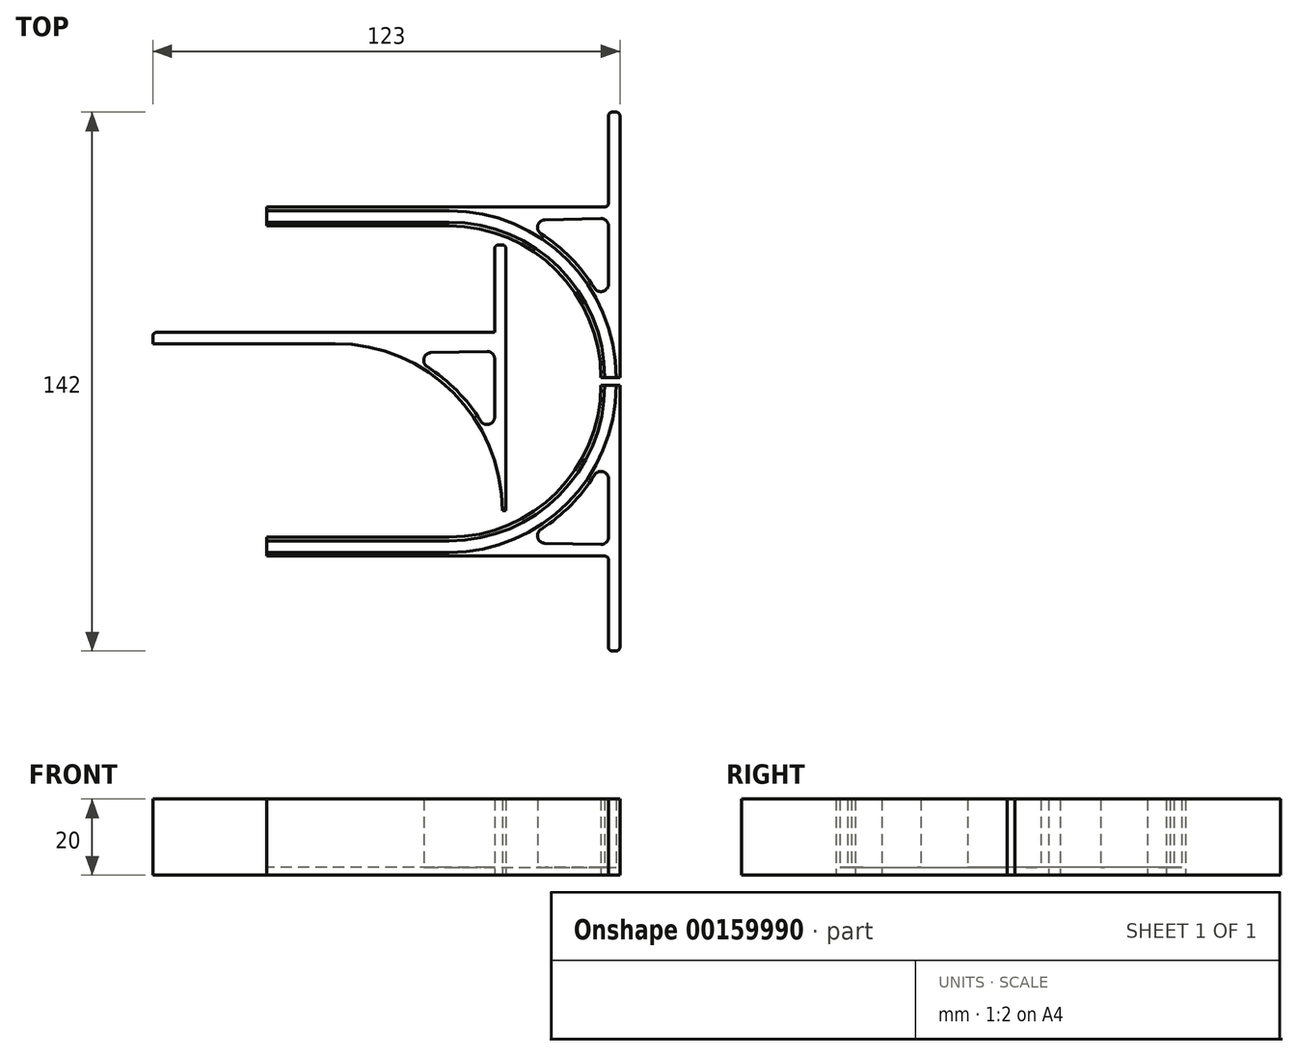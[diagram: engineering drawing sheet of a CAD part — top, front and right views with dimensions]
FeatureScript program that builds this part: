
annotation { "Feature Type Name" : "Feature", "Feature Type Description" : "" }
export const myFeature = defineFeature(function(context is Context, id is Id, definition is map)
    precondition{}
    {
        {
            var Q0;
            Q0=qCreatedBy(makeId("Top.planeOp"),FACE);
            var sketch = newSketch(context, id + "F0", { "sketchPlane" : qUnion([Q0])});
            skLineSegment(sketch, "E0", {"start": v(0, 0) * mm, "end": v(-40, 0) * mm, "construction": true});
            skLineSegment(sketch, "E1", {"start": v(-40, -40) * mm, "end": v(-88, -40) * mm});
            skLineSegment(sketch, "E2", {"start": v(-40, 0) * mm, "end": v(-40, -40) * mm, "construction": true});
            skArc(sketch, "E3", {"start": v(-40, -40) * mm, "mid": v(-11.72, -28.28) * mm, "end": v(0, 0) * mm});
            skLineSegment(sketch, "E4", {"start": v(-88, -40) * mm, "end": v(-88, -45) * mm});
            skLineSegment(sketch, "E5", {"start": v(0, 0) * mm, "end": v(5, 0) * mm});
            skLineSegment(sketch, "E6", {"start": v(5, 0) * mm, "end": v(5, -70) * mm});
            skLineSegment(sketch, "E7", {"start": v(-88, -45) * mm, "end": v(2, -45) * mm});
            skLineSegment(sketch, "E8", {"start": v(2, -45) * mm, "end": v(2, -70) * mm});
            skLineSegment(sketch, "E9", {"start": v(2, -70) * mm, "end": v(5, -70) * mm});
            skSolve(sketch);
        }
        {
            var Q0;
            Q0 = qSketchRegion(id + "F0", true);
            extrude(context, id + "F1", {"entities" : qUnion([Q0]), "depth" : 2 * mm});
        }
        {
            var Q0;
            Q0=makeQuery(id+"F1.opExtrude","CAP_FACE",FACE,{"disambiguationData":[OSD([sQuery(id+"F0.wireOp",EDGE,"E1"),sQuery(id+"F0.wireOp",EDGE,"E3"),sQuery(id+"F0.wireOp",EDGE,"E4"),sQuery(id+"F0.wireOp",EDGE,"E5"),sQuery(id+"F0.wireOp",EDGE,"E6"),sQuery(id+"F0.wireOp",EDGE,"Kue0VMO2-bRpy-jYA9-I0cy-11uejcIptspo"),sQuery(id+"F0.wireOp",EDGE,"twIMW08o-vE7x-7cyn-jqzq-1YqOCdcAmMuu"),sQuery(id+"F0.wireOp",EDGE,"zMnDsJVE-qmB4-Xr0M-Avi3-cOn6qpQtWDXG")])],"isStart":false});
            var sketch = newSketch(context, id + "F2", { "sketchPlane" : qUnion([Q0])});
            skArc(sketch, "E10.0", {"start": v(-40, -40) * mm, "mid": v(-11.72, -28.28) * mm, "end": v(0, 0) * mm});
            skLineSegment(sketch, "E11.0", {"start": v(5, 0) * mm, "end": v(5, 0) * mm});
            skLineSegment(sketch, "E12.0", {"start": v(-40, -40) * mm, "end": v(-88, -40) * mm});
            skLineSegment(sketch, "E13.0", {"start": v(-88, -45) * mm, "end": v(2, -45) * mm});
            skLineSegment(sketch, "E14.0", {"start": v(2, -45) * mm, "end": v(2, -70) * mm});
            skLineSegment(sketch, "E15.0", {"start": v(2, -70) * mm, "end": v(5, -70) * mm});
            skLineSegment(sketch, "E16.0", {"start": v(5, 0) * mm, "end": v(5, -70) * mm});
            skArc(sketch, "E17.0", {"start": v(-40, -41) * mm, "mid": v(-11, -29) * mm, "end": v(1, 0) * mm});
            skLineSegment(sketch, "E18", {"start": v(-40, -41) * mm, "end": v(-88, -41) * mm});
            skPoint(sketch, "E18.endSnap0", {"position": v(-88, -42.5) * mm});
            skLineSegment(sketch, "E19", {"start": v(-88, -40) * mm, "end": v(-88, -41) * mm});
            skLineSegment(sketch, "E20", {"start": v(0, 0) * mm, "end": v(1, 0) * mm});
            skLineSegment(sketch, "E21", {"start": v(5, 0) * mm, "end": v(4, 0) * mm});
            skArc(sketch, "E22", {"start": v(-40, -44) * mm, "mid": v(-8.89, -31.11) * mm, "end": v(4, 0) * mm});
            skLineSegment(sketch, "E23", {"start": v(-40, -44) * mm, "end": v(-88, -44) * mm});
            skLineSegment(sketch, "E24", {"start": v(-88, -44) * mm, "end": v(-88, -45) * mm});
            skArc(sketch, "E25", {"start": v(-40, -45) * mm, "mid": v(-8.18, -31.82) * mm, "end": v(5, 0) * mm});
            skLineSegment(sketch, "E26", {"start": v(2, -42) * mm, "end": v(5, -42) * mm, "construction": true});
            skLineSegment(sketch, "E27", {"start": v(2, -42) * mm, "end": v(2, -45) * mm, "construction": true});
            skLineSegment(sketch, "E28", {"start": v(2, -42) * mm, "end": v(-22.42, -41.43) * mm});
            skLineSegment(sketch, "E29", {"start": v(2, -42) * mm, "end": v(2, -16.16) * mm});
            skSolve(sketch);
        }
        {
            var Q0;
            Q0 = qSketchRegion(id + "F2", true);
            extrude(context, id + "F3", {"entities" : qUnion([Q0]), "operationType" : NewBodyOperationType.ADD, "depth" : 18 * mm});
        }
        {
            var Q0;
            Q0=makeQuery(id+"F3.opExtrude","SWEPT_EDGE",EDGE,{"disambiguationData":[OSD([sQuery(id+"F2.wireOp",EDGE,"E25"),sQuery(id+"F2.wireOp",EDGE,"E28")])]});
            var Q1;
            Q1=makeQuery(id+"F3.opExtrude","SWEPT_EDGE",EDGE,{"disambiguationData":[OSD([sQuery(id+"F2.wireOp",EDGE,"E25"),sQuery(id+"F2.wireOp",EDGE,"E29")])]});
            var Q2;
            Q2=makeQuery(id+"F3.opExtrude","SWEPT_EDGE",EDGE,{"disambiguationData":[OSD([sQuery(id+"F2.wireOp",EDGE,"E28"),sQuery(id+"F2.wireOp",EDGE,"E29")])]});
            fillet(context, id + "F4", {"entities" : qUnion([Q0, Q1, Q2]), "radius" : 2 * mm, "tangentPropagation" : true, "allowEdgeOverflow" : false});
        }
        {
            var Q0;
            Q0=makeQuery(id+"F3.boolean.opBoolean","MERGE",EDGE,{"derivedFrom":[makeQuery(id+"F1.opExtrude","SWEPT_EDGE",EDGE,{"disambiguationData":[OSD([sQuery(id+"F0.wireOp",EDGE,"E8"),sQuery(id+"F0.wireOp",EDGE,"E9")])]}),makeQuery(id+"F3.opExtrude","SWEPT_EDGE",EDGE,{"disambiguationData":[OSD([sQuery(id+"F2.wireOp",EDGE,"E14.0"),sQuery(id+"F2.wireOp",EDGE,"E15.0")])]})]});
            var Q1;
            Q1=makeQuery(id+"F3.boolean.opBoolean","MERGE",EDGE,{"derivedFrom":[makeQuery(id+"F1.opExtrude","SWEPT_EDGE",EDGE,{"disambiguationData":[OSD([sQuery(id+"F0.wireOp",EDGE,"E6"),sQuery(id+"F0.wireOp",EDGE,"E9")])]}),makeQuery(id+"F3.opExtrude","SWEPT_EDGE",EDGE,{"disambiguationData":[OSD([sQuery(id+"F2.wireOp",EDGE,"E15.0"),sQuery(id+"F2.wireOp",EDGE,"E16.0")])]})]});
            fillet(context, id + "F5", {"entities" : qUnion([Q0, Q1]), "radius" : 1 * mm, "tangentPropagation" : true, "allowEdgeOverflow" : false});
        }
        {
            var Q0;
            Q0=makeQuery(id+"F3.boolean.opBoolean","MERGE",FACE,{"derivedFrom":[makeQuery(id+"F1.opExtrude","SWEPT_FACE",FACE,{"disambiguationData":[OSD([sQuery(id+"F0.wireOp",EDGE,"E5")])]}),makeQuery(id+"F3.opExtrude","SWEPT_FACE",FACE,{"disambiguationData":[OSD([sQuery(id+"F2.wireOp",EDGE,"E20")])]}),makeQuery(id+"F3.opExtrude","SWEPT_FACE",FACE,{"disambiguationData":[OSD([sQuery(id+"F2.wireOp",EDGE,"E21")])]})]});
            cPlane(context, id + "F6", {"entities" : qUnion([Q0]), "cplaneType" : CPlaneType.OFFSET, "offset" : 1 * mm, "width" : 150 * mm, "height" : 150 * mm});
        }
        {
            var Q0;
            Q0=makeQuery(id+"F1.opExtrude","SWEPT_BODY",BODY,{"disambiguationData":[OSD([sQuery(id+"F0.wireOp",EDGE,"E1"),sQuery(id+"F0.wireOp",EDGE,"E3"),sQuery(id+"F0.wireOp",EDGE,"E4"),sQuery(id+"F0.wireOp",EDGE,"E5"),sQuery(id+"F0.wireOp",EDGE,"E6"),sQuery(id+"F0.wireOp",EDGE,"E7"),sQuery(id+"F0.wireOp",EDGE,"E8"),sQuery(id+"F0.wireOp",EDGE,"E9")])]});
            var Q1;
            Q1=qCreatedBy(id+"F6.planeOp",FACE);
            mirror(context, id + "F7", {"entities" : qUnion([Q0]), "mirrorPlane" : qUnion([Q1])});
        }
        {
            var Q0;
            Q0=makeQuery(id+"F7.opPattern","COPY",BODY,{"derivedFrom":makeQuery(id+"F1.opExtrude","SWEPT_BODY",BODY,{"disambiguationData":[OSD([sQuery(id+"F0.wireOp",EDGE,"E1"),sQuery(id+"F0.wireOp",EDGE,"E3"),sQuery(id+"F0.wireOp",EDGE,"E4"),sQuery(id+"F0.wireOp",EDGE,"E5"),sQuery(id+"F0.wireOp",EDGE,"E6"),sQuery(id+"F0.wireOp",EDGE,"E7"),sQuery(id+"F0.wireOp",EDGE,"E8"),sQuery(id+"F0.wireOp",EDGE,"E9")])]}),"instanceName":"1"});
            transform(context, id + "F8", {"entities" : qUnion([Q0]), "transformType" : TransformType.TRANSLATION_3D, "dx" : -30 * mm, "dy" : -35 * mm, "dz" : 0 * mm, "makeCopy" : true});
        }
        {
            var Q0;
            {var subQ0=sQuery(id+"F0.wireOp",EDGE,"E5");var subQ1=sQuery(id+"F0.wireOp",EDGE,"E4");Q0=makeQuery(id+"F8.opPattern","COPY",FACE,{"derivedFrom":makeQuery(id+"F7.opPattern","COPY",FACE,{"derivedFrom":makeQuery(id+"F3.boolean.opBoolean","SPLIT",FACE,{"disambiguationData":[TD([makeQuery(id+"F1.opExtrude","SWEPT_FACE",FACE,{"disambiguationData":[OSD([subQ1])]})])],"derivedFrom":makeQuery(id+"F1.opExtrude","CAP_FACE",FACE,{"disambiguationData":[OSD([sQuery(id+"F0.wireOp",EDGE,"E1"),sQuery(id+"F0.wireOp",EDGE,"E3"),subQ1,subQ0,sQuery(id+"F0.wireOp",EDGE,"E6"),sQuery(id+"F0.wireOp",EDGE,"E7"),sQuery(id+"F0.wireOp",EDGE,"E8"),sQuery(id+"F0.wireOp",EDGE,"E9")])],"isStart":false})}),"instanceName":"1"}),"instanceName":"1"});}
            var Q1;
            Q1=makeQuery(id+"F8.opPattern","COPY",FACE,{"derivedFrom":makeQuery(id+"F7.opPattern","COPY",FACE,{"derivedFrom":makeQuery(id+"F3.opExtrude","CAP_FACE",FACE,{"disambiguationData":[OSD([sQuery(id+"F2.wireOp",EDGE,"E10.0"),sQuery(id+"F2.wireOp",EDGE,"E12.0"),sQuery(id+"F2.wireOp",EDGE,"E17.0"),sQuery(id+"F2.wireOp",EDGE,"E18"),sQuery(id+"F2.wireOp",EDGE,"E19"),sQuery(id+"F2.wireOp",EDGE,"E20")])],"isStart":false}),"instanceName":"1"}),"instanceName":"1"});
            extrude(context, id + "F9", {"entities" : qUnion([Q0, Q1]), "operationType" : NewBodyOperationType.REMOVE, "endBound" : BoundingType.THROUGH_ALL, "oppositeDirection" : true, "depth" : 25 * mm});
        }
        {
            var Q0;
            Q0=makeQuery(id+"F8.opPattern","COPY",FACE,{"derivedFrom":makeQuery(id+"F7.opPattern","COPY",FACE,{"derivedFrom":makeQuery(id+"F3.boolean.opBoolean","MERGE",FACE,{"derivedFrom":[makeQuery(id+"F1.opExtrude","SWEPT_FACE",FACE,{"disambiguationData":[OSD([sQuery(id+"F0.wireOp",EDGE,"E7")])]}),makeQuery(id+"F3.opExtrude","SWEPT_FACE",FACE,{"disambiguationData":[OSD([sQuery(id+"F2.wireOp",EDGE,"E13.0")])]})]}),"instanceName":"1"}),"instanceName":"1"});
            extrude(context, id + "F10", {"entities" : qUnion([Q0]), "operationType" : NewBodyOperationType.ADD, "depth" : 2 * mm});
        }
        {
            var Q0;
            Q0=makeQuery(id+"F3.boolean.opBoolean","MERGE",EDGE,{"derivedFrom":[makeQuery(id+"F1.opExtrude","SWEPT_EDGE",EDGE,{"disambiguationData":[OSD([sQuery(id+"F0.wireOp",EDGE,"E7"),sQuery(id+"F0.wireOp",EDGE,"E8")])]}),makeQuery(id+"F3.opExtrude","SWEPT_EDGE",EDGE,{"disambiguationData":[OSD([sQuery(id+"F2.wireOp",EDGE,"E13.0"),sQuery(id+"F2.wireOp",EDGE,"E14.0")])]})]});
            var Q1;
            Q1=makeQuery(id+"F10.opExtrude","CAP_EDGE",EDGE,{"disambiguationData":[OSD([sQuery(id+"F0.wireOp",EDGE,"E7"),sQuery(id+"F0.wireOp",EDGE,"E8"),sQuery(id+"F2.wireOp",EDGE,"E13.0"),sQuery(id+"F2.wireOp",EDGE,"E14.0")])],"isStart":false});
            var Q2;
            Q2=makeQuery(id+"F7.opPattern","COPY",EDGE,{"derivedFrom":makeQuery(id+"F3.boolean.opBoolean","MERGE",EDGE,{"derivedFrom":[makeQuery(id+"F1.opExtrude","SWEPT_EDGE",EDGE,{"disambiguationData":[OSD([sQuery(id+"F0.wireOp",EDGE,"E7"),sQuery(id+"F0.wireOp",EDGE,"E8")])]}),makeQuery(id+"F3.opExtrude","SWEPT_EDGE",EDGE,{"disambiguationData":[OSD([sQuery(id+"F2.wireOp",EDGE,"E13.0"),sQuery(id+"F2.wireOp",EDGE,"E14.0")])]})]}),"instanceName":"1"});
            var Q3;
            Q3=makeQuery(id+"F10.opExtrude","CAP_EDGE",EDGE,{"disambiguationData":[OSD([sQuery(id+"F0.wireOp",EDGE,"E4"),sQuery(id+"F0.wireOp",EDGE,"E7"),sQuery(id+"F2.wireOp",EDGE,"E13.0"),sQuery(id+"F2.wireOp",EDGE,"E24")])],"isStart":false});
            var Q4;
            {var subQ0=sQuery(id+"F2.wireOp",EDGE,"E24");var subQ1=sQuery(id+"F2.wireOp",EDGE,"E23");var subQ2=sQuery(id+"F0.wireOp",EDGE,"E4");Q4=makeQuery(id+"F9.boolean.opBoolean","MERGE",EDGE,{"derivedFrom":[makeQuery(id+"F8.opPattern","COPY",EDGE,{"derivedFrom":makeQuery(id+"F7.opPattern","COPY",EDGE,{"derivedFrom":makeQuery(id+"F3.opExtrude","SWEPT_EDGE",EDGE,{"disambiguationData":[OSD([subQ2,subQ1,subQ0])]}),"instanceName":"1"}),"instanceName":"1"}),makeQuery(id+"F9.opExtrude","SWEPT_EDGE",EDGE,{"disambiguationData":[OSD([subQ2,subQ1,subQ0])]})]});}
            fillet(context, id + "F11", {"entities" : qUnion([Q0, Q1, Q2, Q3, Q4]), "radius" : 1 * mm, "tangentPropagation" : true, "allowEdgeOverflow" : false});
        }
    });
